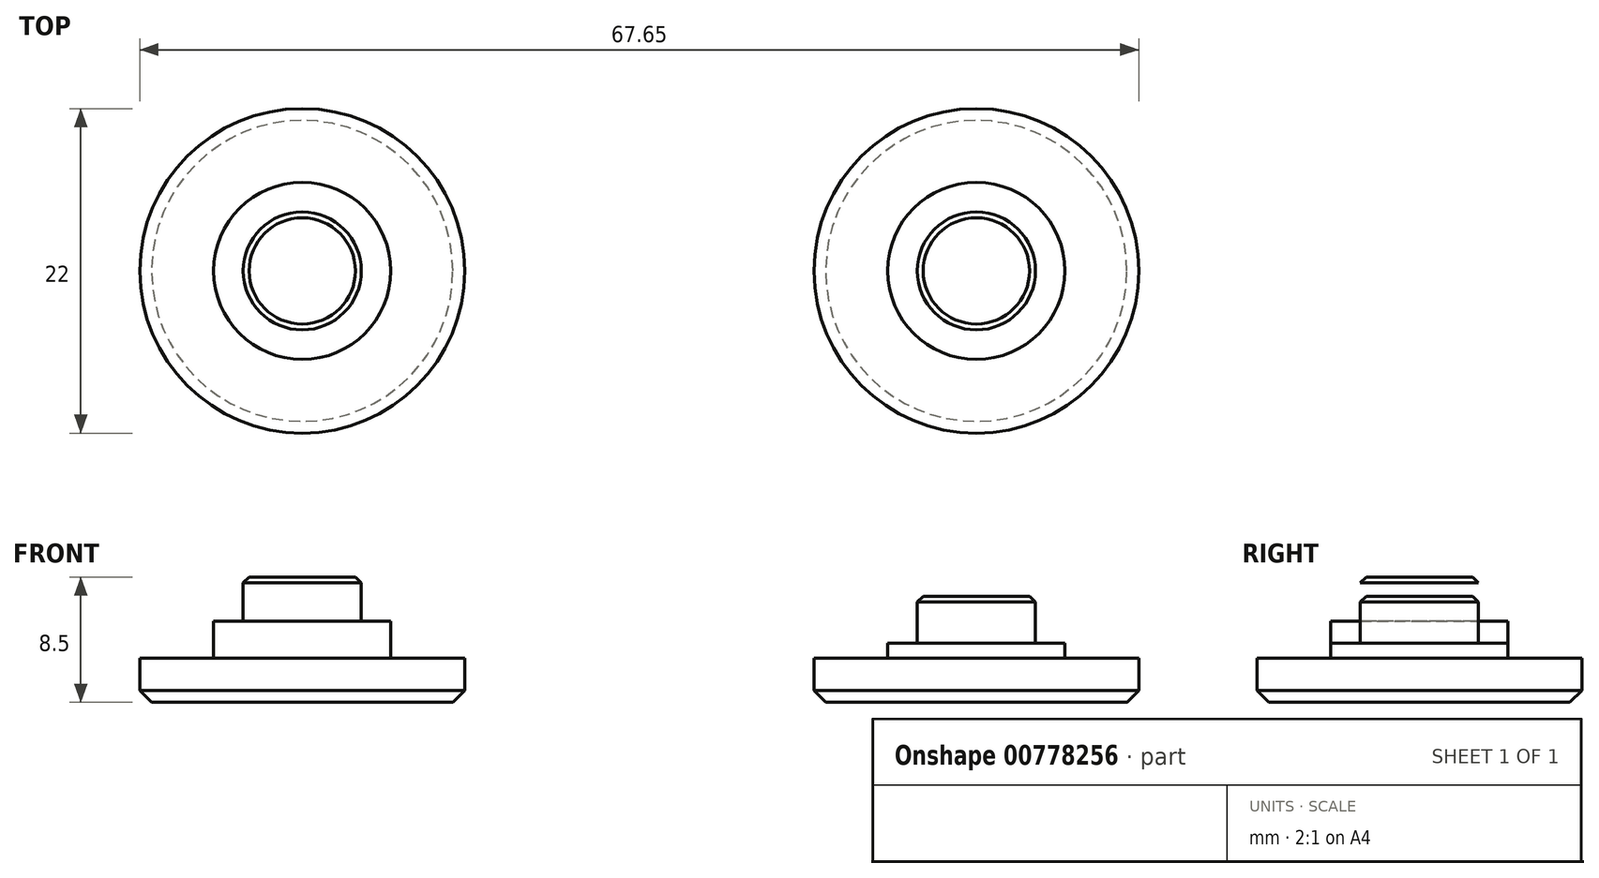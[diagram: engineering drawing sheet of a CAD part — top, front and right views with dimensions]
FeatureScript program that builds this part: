
annotation { "Feature Type Name" : "Feature", "Feature Type Description" : "" }
export const myFeature = defineFeature(function(context is Context, id is Id, definition is map)
    precondition{}
    {
        {
            var Q0;
            Q0=qCreatedBy(makeId("Top.planeOp"),FACE);
            var sketch = newSketch(context, id + "F0", { "sketchPlane" : qUnion([Q0])});
            skCircle(sketch, "E0", {"center": v(0, 0) * mm, "radius": 11 * mm});
            skCircle(sketch, "E1", {"center": v(0, 0) * mm, "radius": 6 * mm});
            skCircle(sketch, "E2", {"center": v(0, 0) * mm, "radius": 4 * mm});
            skCircle(sketch, "E3", {"center": v(-45.65, 0) * mm, "radius": 11 * mm});
            skCircle(sketch, "E4", {"center": v(-45.65, 0) * mm, "radius": 6 * mm});
            skCircle(sketch, "E5", {"center": v(-45.65, 0) * mm, "radius": 4 * mm});
            skSolve(sketch);
        }
        {
            var Q0;
            Q0=makeQuery(id+"F0.imprint","IMPRINT",FACE,{"disambiguationData":[TD([[makeQuery(id+"F0.imprint","IMPRINT",EDGE,{"derivedFrom":sQuery(id+"F0.wireOp",EDGE,"E3")}),1.0]])]});
            var Q1;
            Q1=makeQuery(id+"F0.imprint","IMPRINT",FACE,{"disambiguationData":[TD([[makeQuery(id+"F0.imprint","IMPRINT",EDGE,{"derivedFrom":sQuery(id+"F0.wireOp",EDGE,"E5")}),1.0]])]});
            var Q2;
            Q2=makeQuery(id+"F0.imprint","IMPRINT",FACE,{"disambiguationData":[TD([[makeQuery(id+"F0.imprint","IMPRINT",EDGE,{"derivedFrom":sQuery(id+"F0.wireOp",EDGE,"E4")}),1.0]])]});
            extrude(context, id + "F1", {"entities" : qUnion([Q0, Q1, Q2]), "depth" : 3 * mm, "offsetDistance" : 25 * mm});
        }
        {
            var Q0;
            Q0=makeQuery(id+"F0.imprint","IMPRINT",FACE,{"disambiguationData":[TD([[makeQuery(id+"F0.imprint","IMPRINT",EDGE,{"derivedFrom":sQuery(id+"F0.wireOp",EDGE,"E4")}),1.0]])]});
            var Q1;
            Q1=makeQuery(id+"F0.imprint","IMPRINT",FACE,{"disambiguationData":[TD([[makeQuery(id+"F0.imprint","IMPRINT",EDGE,{"derivedFrom":sQuery(id+"F0.wireOp",EDGE,"E5")}),1.0]])]});
            extrude(context, id + "F2", {"entities" : qUnion([Q0, Q1]), "operationType" : NewBodyOperationType.ADD, "depth" : 5.5 * mm, "offsetDistance" : 25 * mm});
        }
        {
            var Q0;
            Q0=makeQuery(id+"F0.imprint","IMPRINT",FACE,{"disambiguationData":[TD([[makeQuery(id+"F0.imprint","IMPRINT",EDGE,{"derivedFrom":sQuery(id+"F0.wireOp",EDGE,"E5")}),1.0]])]});
            extrude(context, id + "F3", {"entities" : qUnion([Q0]), "operationType" : NewBodyOperationType.ADD, "depth" : 8.5 * mm, "offsetDistance" : 25 * mm});
        }
        {
            var Q0;
            Q0=makeQuery(id+"F0.imprint","IMPRINT",FACE,{"disambiguationData":[TD([[makeQuery(id+"F0.imprint","IMPRINT",EDGE,{"derivedFrom":sQuery(id+"F0.wireOp",EDGE,"E0")}),1.0]])]});
            var Q1;
            Q1=makeQuery(id+"F0.imprint","IMPRINT",FACE,{"disambiguationData":[TD([[makeQuery(id+"F0.imprint","IMPRINT",EDGE,{"derivedFrom":sQuery(id+"F0.wireOp",EDGE,"E1")}),1.0]])]});
            var Q2;
            Q2=makeQuery(id+"F0.imprint","IMPRINT",FACE,{"disambiguationData":[TD([[makeQuery(id+"F0.imprint","IMPRINT",EDGE,{"derivedFrom":sQuery(id+"F0.wireOp",EDGE,"E2")}),1.0]])]});
            extrude(context, id + "F4", {"entities" : qUnion([Q0, Q1, Q2]), "depth" : 3 * mm, "offsetDistance" : 25 * mm});
        }
        {
            var Q0;
            Q0=makeQuery(id+"F0.imprint","IMPRINT",FACE,{"disambiguationData":[TD([[makeQuery(id+"F0.imprint","IMPRINT",EDGE,{"derivedFrom":sQuery(id+"F0.wireOp",EDGE,"E2")}),1.0]])]});
            var Q1;
            Q1=makeQuery(id+"F0.imprint","IMPRINT",FACE,{"disambiguationData":[TD([[makeQuery(id+"F0.imprint","IMPRINT",EDGE,{"derivedFrom":sQuery(id+"F0.wireOp",EDGE,"E1")}),1.0]])]});
            extrude(context, id + "F5", {"entities" : qUnion([Q0, Q1]), "operationType" : NewBodyOperationType.ADD, "depth" : 4 * mm, "offsetDistance" : 25 * mm});
        }
        {
            var Q0;
            Q0=makeQuery(id+"F0.imprint","IMPRINT",FACE,{"disambiguationData":[TD([[makeQuery(id+"F0.imprint","IMPRINT",EDGE,{"derivedFrom":sQuery(id+"F0.wireOp",EDGE,"E2")}),1.0]])]});
            extrude(context, id + "F6", {"entities" : qUnion([Q0]), "operationType" : NewBodyOperationType.ADD, "depth" : 7.2 * mm, "offsetDistance" : 25 * mm});
        }
        {
            var Q0;
            Q0=makeQuery(id+"F1.opExtrude","CAP_EDGE",EDGE,{"disambiguationData":[OSD([sQuery(id+"F0.wireOp",EDGE,"E3")])],"isStart":true});
            var Q1;
            Q1=makeQuery(id+"F4.opExtrude","CAP_EDGE",EDGE,{"disambiguationData":[OSD([sQuery(id+"F0.wireOp",EDGE,"E0")])],"isStart":true});
            chamfer(context, id + "F7", {"entities" : qUnion([Q0, Q1]), "width" : 0.8 * mm, "tangentPropagation" : true});
        }
        {
            var Q0;
            Q0=makeQuery(id+"F3.opExtrude","CAP_EDGE",EDGE,{"disambiguationData":[OSD([sQuery(id+"F0.wireOp",EDGE,"E5")])],"isStart":false});
            var Q1;
            Q1=makeQuery(id+"F6.opExtrude","CAP_EDGE",EDGE,{"disambiguationData":[OSD([sQuery(id+"F0.wireOp",EDGE,"E2")])],"isStart":false});
            chamfer(context, id + "F8", {"entities" : qUnion([Q0, Q1]), "width" : 0.4 * mm, "tangentPropagation" : true});
        }
    });
